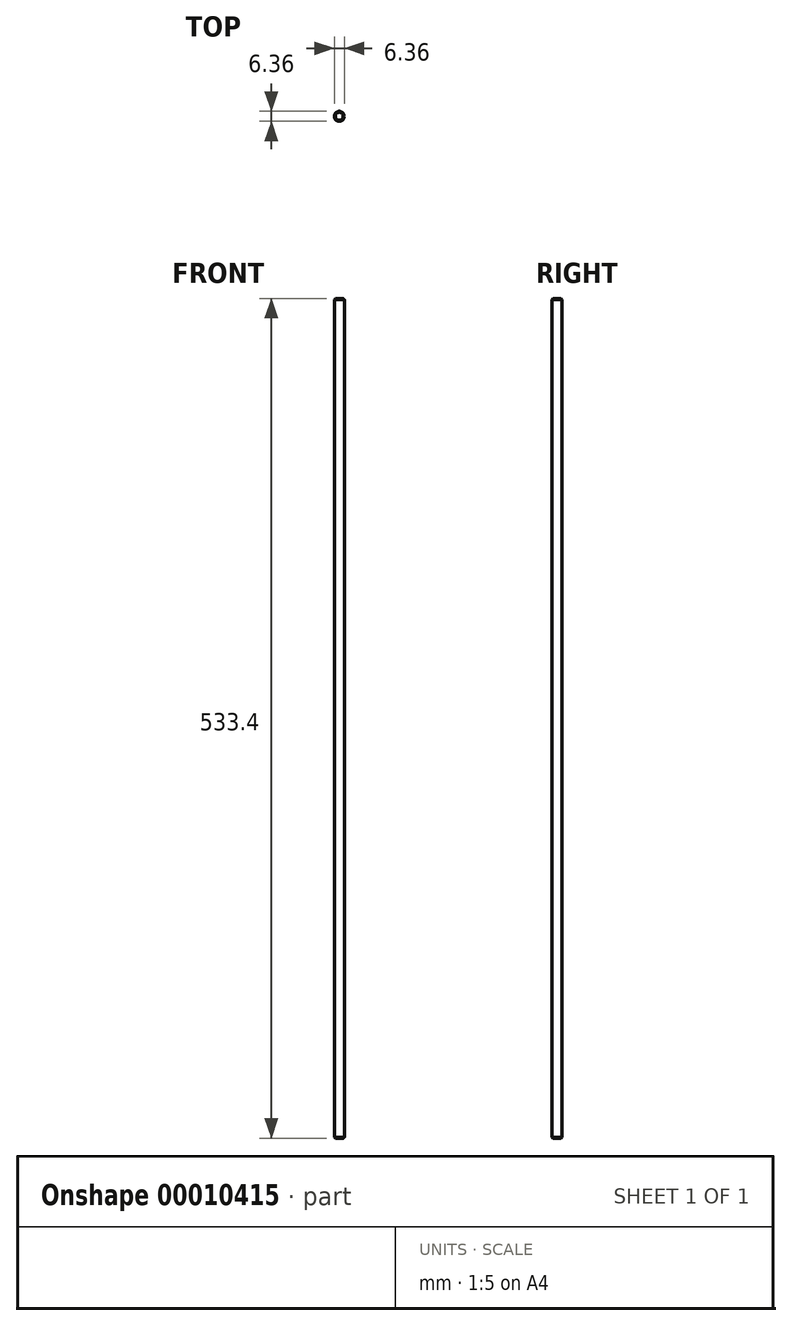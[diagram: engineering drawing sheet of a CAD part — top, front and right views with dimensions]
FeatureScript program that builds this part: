
annotation { "Feature Type Name" : "Feature", "Feature Type Description" : "" }
export const myFeature = defineFeature(function(context is Context, id is Id, definition is map)
    precondition{}
    {
        {
            var Q0;
            Q0=qCreatedBy(makeId("Top.planeOp"),FACE);
            var sketch = newSketch(context, id + "F0", { "sketchPlane" : qUnion([Q0])});
            skCircle(sketch, "E0", {"center": v(0, 0) * mm, "radius": 3.18 * mm});
            skSolve(sketch);
        }
        {
            var Q0;
            Q0=makeQuery(id+"F0.imprint","IMPRINT",FACE,{"disambiguationData":[TD([[makeQuery(id+"F0.imprint","IMPRINT",EDGE,{"derivedFrom":sQuery(id+"F0.wireOp",EDGE,"E0")}),1.0]])]});
            extrude(context, id + "F1", {"entities" : qUnion([Q0]), "endBound" : BoundingType.SYMMETRIC, "depth" : 533.4 * mm});
        }
        {
            var Q0;
            Q0=makeQuery(id+"F1.opExtrude","CAP_EDGE",EDGE,{"disambiguationData":[OSD([sQuery(id+"F0.wireOp",EDGE,"E0")])],"isStart":false});
            chamfer(context, id + "F2", {"entities" : qUnion([Q0]), "width" : 0.64 * mm, "tangentPropagation" : true});
        }
        {
            var Q0;
            Q0=makeQuery(id+"F1.opExtrude","CAP_EDGE",EDGE,{"disambiguationData":[OSD([sQuery(id+"F0.wireOp",EDGE,"E0")])],"isStart":true});
            chamfer(context, id + "F3", {"entities" : qUnion([Q0]), "width" : 0.64 * mm, "tangentPropagation" : true});
        }
    });
